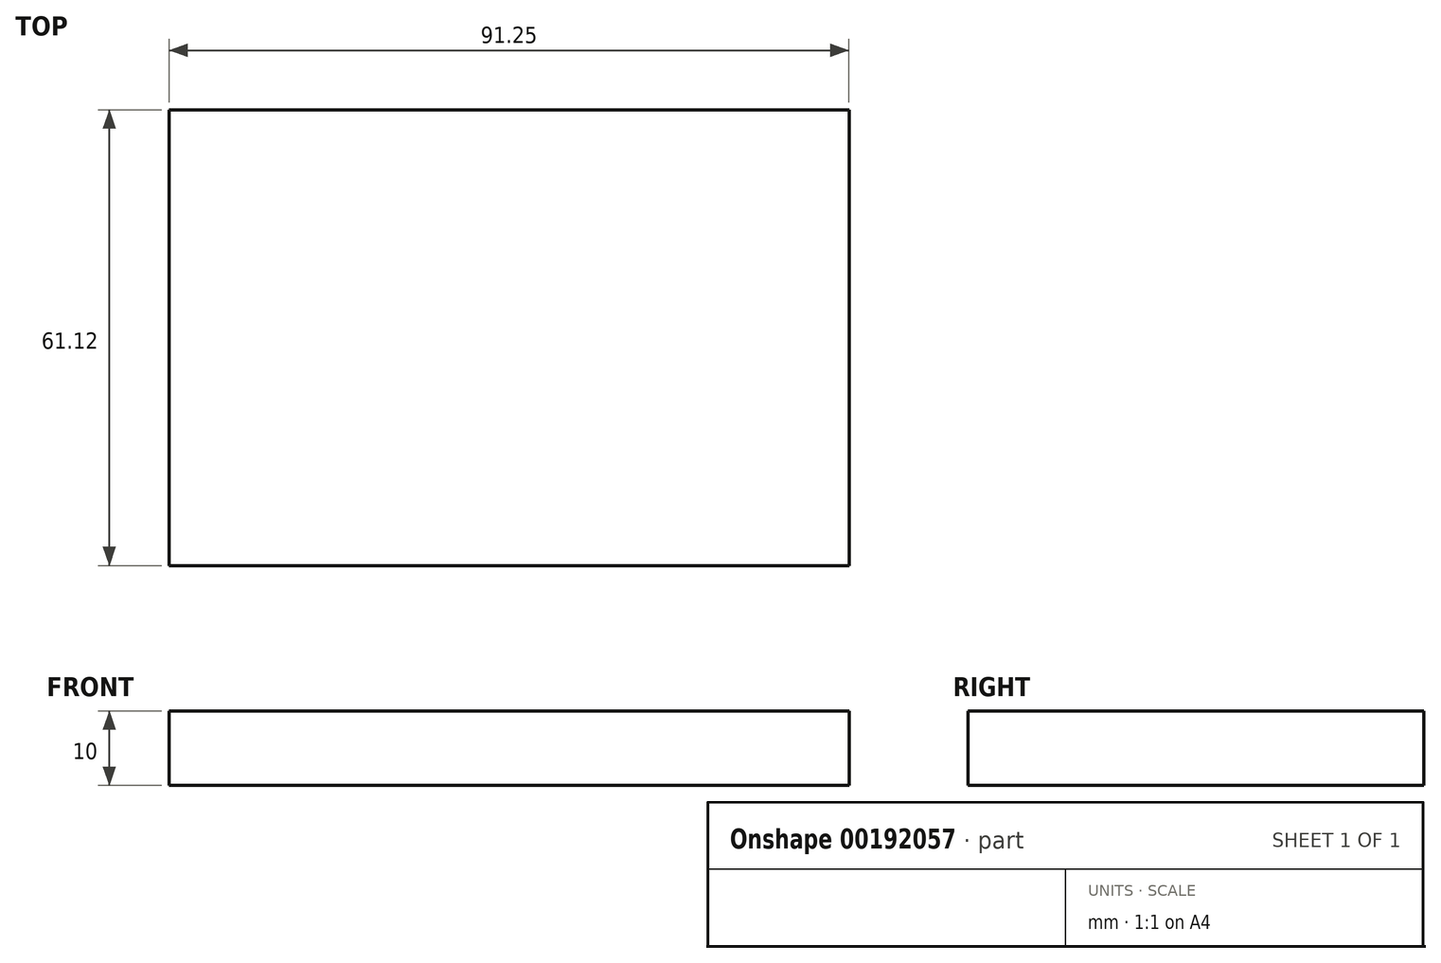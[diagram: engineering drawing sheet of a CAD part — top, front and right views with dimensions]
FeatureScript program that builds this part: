
annotation { "Feature Type Name" : "Feature", "Feature Type Description" : "" }
export const myFeature = defineFeature(function(context is Context, id is Id, definition is map)
    precondition{}
    {
        {
            var Q0;
            Q0=qCreatedBy(makeId("Top.planeOp"),FACE);
            var sketch = newSketch(context, id + "F0", { "sketchPlane" : qUnion([Q0])});
            skLineSegment(sketch, "E0.bottom", {"start": v(-32.53, 23.03) * mm, "end": v(58.72, 23.03) * mm});
            skLineSegment(sketch, "E0.top", {"start": v(-32.53, -38.1) * mm, "end": v(58.72, -38.1) * mm});
            skLineSegment(sketch, "E0.left", {"start": v(-32.53, 23.03) * mm, "end": v(-32.53, -38.1) * mm});
            skLineSegment(sketch, "E0.right", {"start": v(58.72, 23.03) * mm, "end": v(58.72, -38.1) * mm});
            skSolve(sketch);
        }
        {
            var Q0;
            Q0 = qSketchRegion(id + "F0", true);
            extrude(context, id + "F1", {"entities" : qUnion([Q0]), "depth" : 10 * mm});
        }
    });
